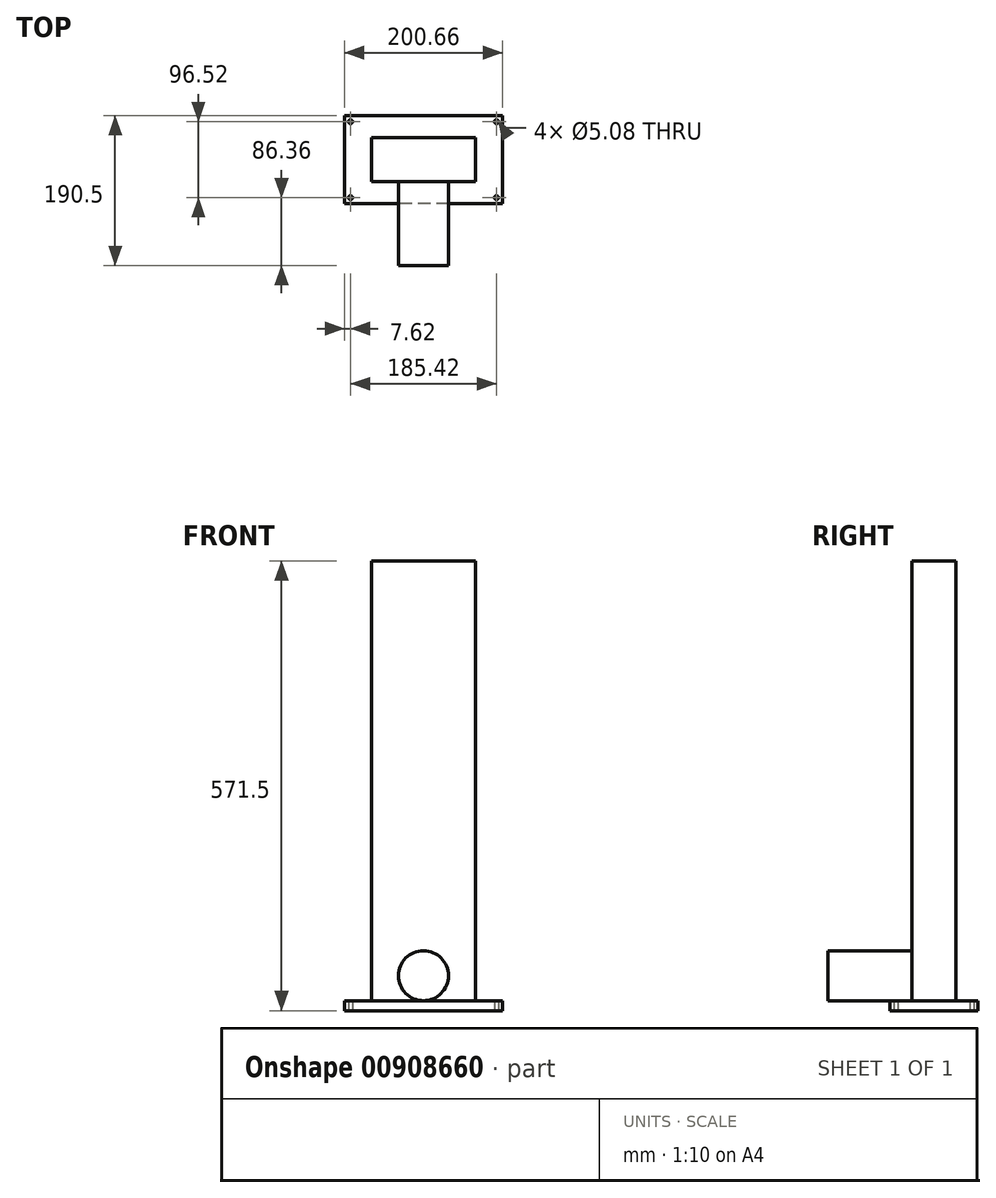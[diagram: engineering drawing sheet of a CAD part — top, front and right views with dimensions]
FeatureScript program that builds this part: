
annotation { "Feature Type Name" : "Feature", "Feature Type Description" : "" }
export const myFeature = defineFeature(function(context is Context, id is Id, definition is map)
    precondition{}
    {
        {
            var Q0;
            Q0=qCreatedBy(makeId("Top.planeOp"),FACE);
            var sketch = newSketch(context, id + "F0", { "sketchPlane" : qUnion([Q0])});
            skLineSegment(sketch, "E0.bottom", {"start": v(100.33, 55.88) * mm, "end": v(-100.33, 55.88) * mm});
            skLineSegment(sketch, "E0.top", {"start": v(100.33, -55.88) * mm, "end": v(-100.33, -55.88) * mm});
            skLineSegment(sketch, "E0.left", {"start": v(100.33, 55.88) * mm, "end": v(100.33, -55.88) * mm});
            skLineSegment(sketch, "E0.right", {"start": v(-100.33, 55.88) * mm, "end": v(-100.33, -55.88) * mm});
            skPoint(sketch, "E0.middle", {"position": v(0, 0) * mm});
            skCircle(sketch, "E1", {"center": v(-92.71, 48.26) * mm, "radius": 2.54 * mm});
            skLineSegment(sketch, "E2", {"start": v(-100.33, 0) * mm, "end": v(100.33, 0) * mm, "construction": true});
            skLineSegment(sketch, "E3", {"start": v(0, 55.88) * mm, "end": v(0, -55.88) * mm, "construction": true});
            skCircle(sketch, "E4.MirrorC", {"center": v(92.71, 48.26) * mm, "radius": 2.54 * mm});
            skCircle(sketch, "E5.MirrorC", {"center": v(-92.71, -48.26) * mm, "radius": 2.54 * mm});
            skCircle(sketch, "E6.MirrorC", {"center": v(92.71, -48.26) * mm, "radius": 2.54 * mm});
            skSolve(sketch);
        }
        {
            var Q0;
            Q0=makeQuery(id+"F0.imprint","IMPRINT",FACE,{"disambiguationData":[TD([[makeQuery(id+"F0.imprint","IMPRINT",EDGE,{"derivedFrom":sQuery(id+"F0.wireOp",EDGE,"E0.bottom")}),1.0]])]});
            extrude(context, id + "F1", {"entities" : qUnion([Q0]), "depth" : 12.7 * mm, "offsetDistance" : 25.4 * mm});
        }
        {
            var Q0;
            Q0=makeQuery(id+"F1.opExtrude","CAP_FACE",FACE,{"disambiguationData":[OSD([sQuery(id+"F0.wireOp",EDGE,"E0.bottom"),sQuery(id+"F0.wireOp",EDGE,"E0.top"),sQuery(id+"F0.wireOp",EDGE,"E0.left"),sQuery(id+"F0.wireOp",EDGE,"E0.right"),sQuery(id+"F0.wireOp",EDGE,"E1"),sQuery(id+"F0.wireOp",EDGE,"E4.MirrorC"),sQuery(id+"F0.wireOp",EDGE,"E5.MirrorC"),sQuery(id+"F0.wireOp",EDGE,"E6.MirrorC")])],"isStart":false});
            var sketch = newSketch(context, id + "F2", { "sketchPlane" : qUnion([Q0])});
            skLineSegment(sketch, "E7.bottom", {"start": v(66.04, 27.94) * mm, "end": v(-66.04, 27.94) * mm});
            skLineSegment(sketch, "E7.top", {"start": v(66.04, -27.94) * mm, "end": v(-66.04, -27.94) * mm});
            skLineSegment(sketch, "E7.left", {"start": v(66.04, 27.94) * mm, "end": v(66.04, -27.94) * mm});
            skLineSegment(sketch, "E7.right", {"start": v(-66.04, 27.94) * mm, "end": v(-66.04, -27.94) * mm});
            skPoint(sketch, "E7.middle", {"position": v(0, 0) * mm});
            skSolve(sketch);
        }
        {
            var Q0;
            Q0=qSketchRegion(id+"F2",true);
            extrude(context, id + "F3", {"entities" : qUnion([Q0]), "operationType" : NewBodyOperationType.ADD, "depth" : 609.6 * mm - 50.8 * mm, "offsetDistance" : 25.4 * mm});
        }
        {
            var Q0;
            Q0=makeQuery(id+"F3.opExtrude","SWEPT_FACE",FACE,{"disambiguationData":[OSD([sQuery(id+"F2.wireOp",EDGE,"E7.top")])]});
            var sketch = newSketch(context, id + "F4", { "sketchPlane" : qUnion([Q0])});
            skCircle(sketch, "E8", {"center": v(0, 44.45) * mm, "radius": 31.75 * mm});
            skPoint(sketch, "E8.centerSnap0", {"position": v(0, 12.7) * mm});
            skSolve(sketch);
        }
        {
            var Q0;
            Q0=qSketchRegion(id+"F4",true);
            extrude(context, id + "F5", {"entities" : qUnion([Q0]), "depth" : 106.68 * mm, "offsetDistance" : 25.4 * mm});
        }
    });
